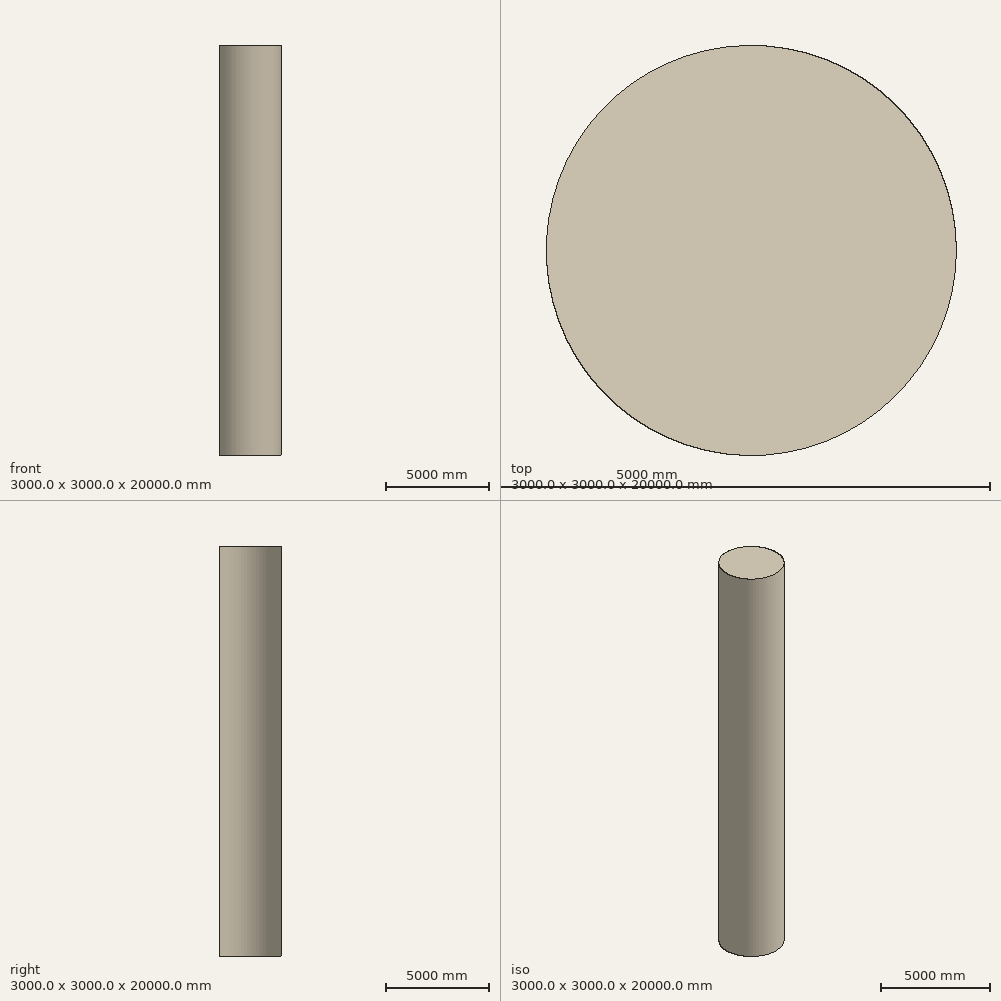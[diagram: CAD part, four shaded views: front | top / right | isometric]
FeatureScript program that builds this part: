
annotation { "Feature Type Name" : "Feature", "Feature Type Description" : "" }
export const myFeature = defineFeature(function(context is Context, id is Id, definition is map)
    precondition{}
    {
        {
            var Q0;
            Q0=qCreatedBy(makeId("Top.planeOp"),FACE);
            var sketch = newSketch(context, id + "F0", { "sketchPlane" : qUnion([Q0])});
            skCircle(sketch, "E0", {"center": v(0, 0) * mm, "radius": 1500 * mm});
            skSolve(sketch);
        }
        {
            var Q0;
            Q0=makeQuery(id+"F0.imprint","IMPRINT",FACE,{"disambiguationData":[TD([[makeQuery(id+"F0.imprint","IMPRINT",EDGE,{"derivedFrom":sQuery(id+"F0.wireOp",EDGE,"E0")}),1.0]])]});
            extrude(context, id + "F1", {"entities" : qUnion([Q0]), "oppositeDirection" : true, "depth" : 20000 * mm, "offsetDistance" : 25 * mm});
        }
    });
